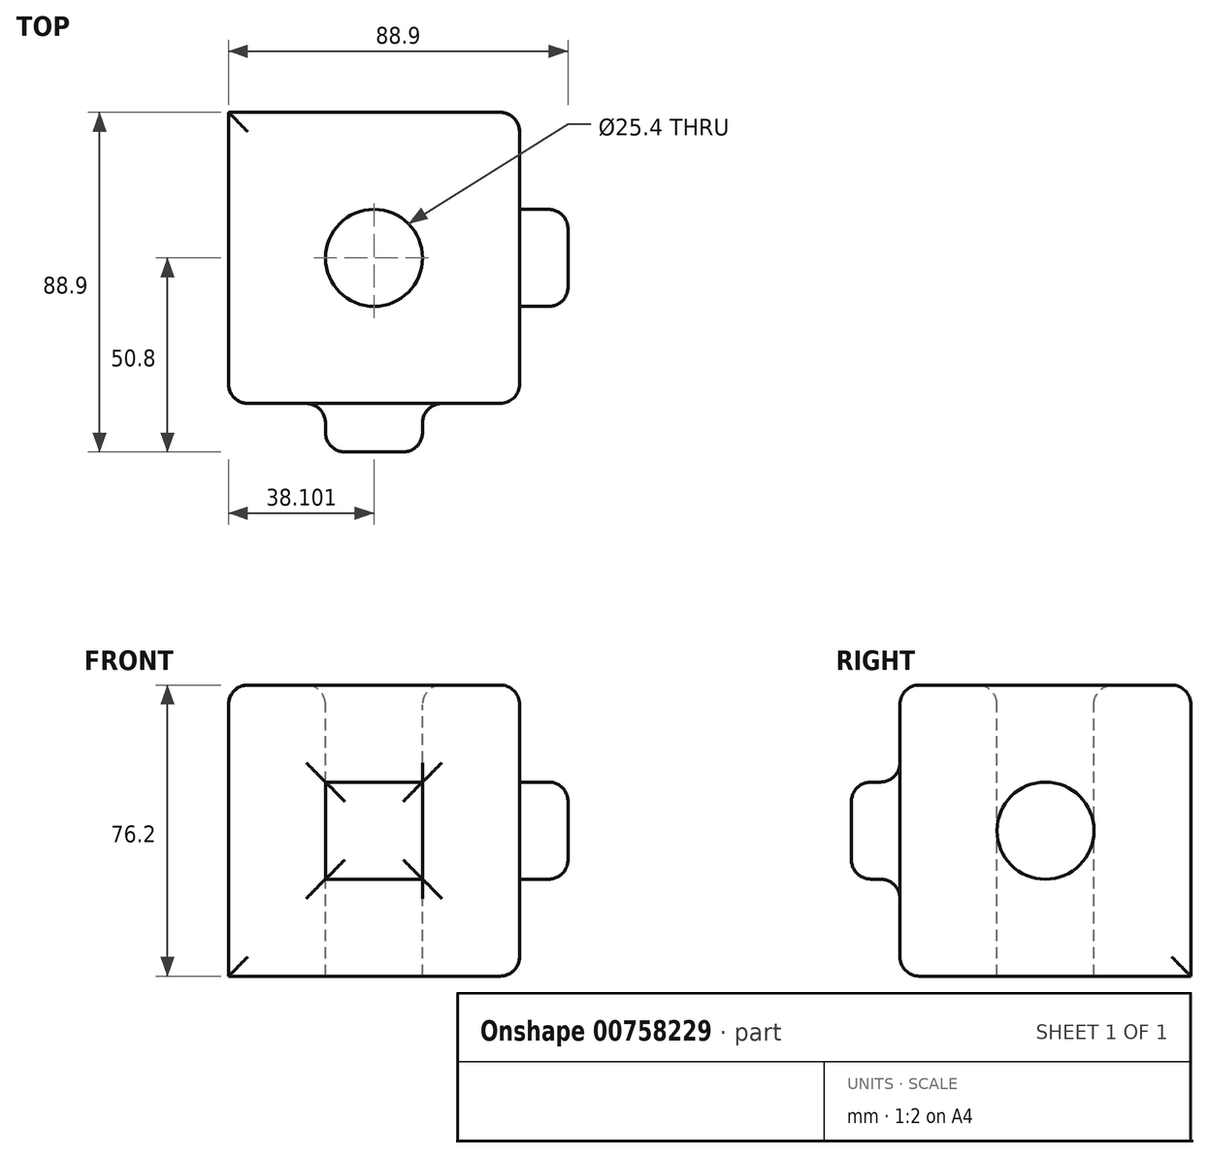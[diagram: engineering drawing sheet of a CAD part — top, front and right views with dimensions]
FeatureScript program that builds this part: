
annotation { "Feature Type Name" : "Feature", "Feature Type Description" : "" }
export const myFeature = defineFeature(function(context is Context, id is Id, definition is map)
    precondition{}
    {
        {
            var Q0;
            Q0=qCreatedBy(makeId("Front.planeOp"),FACE);
            var sketch = newSketch(context, id + "F0", { "sketchPlane" : qUnion([Q0])});
            skLineSegment(sketch, "E0.bottom", {"start": v(-584.28, 76.45) * mm, "end": v(-508.08, 76.45) * mm});
            skLineSegment(sketch, "E0.top", {"start": v(-584.28, 152.65) * mm, "end": v(-508.08, 152.65) * mm});
            skLineSegment(sketch, "E0.left", {"start": v(-584.28, 76.45) * mm, "end": v(-584.28, 152.65) * mm});
            skLineSegment(sketch, "E0.right", {"start": v(-508.08, 76.45) * mm, "end": v(-508.08, 152.65) * mm});
            skSolve(sketch);
        }
        {
            var Q0;
            Q0 = qSketchRegion(id + "F0", true);
            extrude(context, id + "F1", {"entities" : qUnion([Q0]), "depth" : 76.2 * mm, "offsetDistance" : 25.4 * mm});
        }
        {
            var Q0;
            Q0=makeQuery(id+"F1.opExtrude","SWEPT_FACE",FACE,{"disambiguationData":[OSD([sQuery(id+"F0.wireOp",EDGE,"E0.top")])]});
            var sketch = newSketch(context, id + "F2", { "sketchPlane" : qUnion([Q0])});
            skPoint(sketch, "E1", {"position": v(-546.18, -38.1) * mm});
            skPoint(sketch, "E1.positionSnap0", {"position": v(-508.08, -38.1) * mm});
            skPoint(sketch, "E1.positionSnap1", {"position": v(-546.18, 0) * mm});
            skSolve(sketch);
        }
        {
            var Q0;
            Q0=sQuery(id+"F2.wireOp",VERTEX,"E1");
            var Q1;
            Q1=makeQuery(id+"F1.opExtrude","SWEPT_BODY",BODY,{"disambiguationData":[OSD([sQuery(id+"F0.wireOp",EDGE,"E0.bottom"),sQuery(id+"F0.wireOp",EDGE,"E0.top"),sQuery(id+"F0.wireOp",EDGE,"E0.left"),sQuery(id+"F0.wireOp",EDGE,"E0.right")])]});
            hole(context, id + "F3", {"style" : HoleStyle.SIMPLE, "endStyle" : HoleEndStyle.THROUGH, "holeDiameter" : 25.4 * mm, "majorDiameter" : 6.35 * mm, "isTappedThrough" : true, "tappedDepth" : 12.7 * mm, "tapClearance" : 3, "locations" : qUnion([Q0]), "scope" : qUnion([Q1])});
        }
        {
            var Q0;
            Q0=makeQuery(id+"F1.opExtrude","CAP_FACE",FACE,{"disambiguationData":[OSD([sQuery(id+"F0.wireOp",EDGE,"E0.bottom"),sQuery(id+"F0.wireOp",EDGE,"E0.top"),sQuery(id+"F0.wireOp",EDGE,"E0.left"),sQuery(id+"F0.wireOp",EDGE,"E0.right")])],"isStart":false});
            var sketch = newSketch(context, id + "F4", { "sketchPlane" : qUnion([Q0])});
            skPoint(sketch, "E2", {"position": v(-546.18, 114.55) * mm});
            skPoint(sketch, "E2.positionSnap0", {"position": v(-508.08, 114.55) * mm});
            skPoint(sketch, "E2.positionSnap1", {"position": v(-546.18, 152.65) * mm});
            skLineSegment(sketch, "E3.bottom", {"start": v(-533.48, 127.25) * mm, "end": v(-558.88, 127.25) * mm});
            skLineSegment(sketch, "E3.top", {"start": v(-533.48, 101.85) * mm, "end": v(-558.88, 101.85) * mm});
            skLineSegment(sketch, "E3.left", {"start": v(-533.48, 127.25) * mm, "end": v(-533.48, 101.85) * mm});
            skLineSegment(sketch, "E3.right", {"start": v(-558.88, 127.25) * mm, "end": v(-558.88, 101.85) * mm});
            skSolve(sketch);
        }
        {
            var Q0;
            Q0 = qSketchRegion(id + "F4", true);
            extrude(context, id + "F5", {"entities" : qUnion([Q0]), "operationType" : NewBodyOperationType.ADD, "depth" : 12.7 * mm, "offsetDistance" : 25.4 * mm});
        }
        {
            var Q0;
            Q0=makeQuery(id+"F1.opExtrude","SWEPT_FACE",FACE,{"disambiguationData":[OSD([sQuery(id+"F0.wireOp",EDGE,"E0.right")])]});
            var sketch = newSketch(context, id + "F6", { "sketchPlane" : qUnion([Q0])});
            skPoint(sketch, "E4", {"position": v(-38.1, 114.55) * mm});
            skPoint(sketch, "E4.positionSnap0", {"position": v(0, 114.55) * mm});
            skPoint(sketch, "E4.positionSnap1", {"position": v(-38.1, 152.65) * mm});
            skCircle(sketch, "E5", {"center": v(-38.1, 114.55) * mm, "radius": 12.7 * mm});
            skSolve(sketch);
        }
        {
            var Q0;
            Q0 = qSketchRegion(id + "F6", true);
            extrude(context, id + "F7", {"entities" : qUnion([Q0]), "operationType" : NewBodyOperationType.ADD, "depth" : 12.7 * mm, "offsetDistance" : 25.4 * mm});
        }
        {
            var Q0;
            Q0=makeQuery(id+"F1.opExtrude","CAP_EDGE",EDGE,{"disambiguationData":[OSD([sQuery(id+"F0.wireOp",EDGE,"E0.top")])],"isStart":false});
            var Q1;
            Q1=makeQuery(id+"F1.opExtrude","SWEPT_EDGE",EDGE,{"disambiguationData":[OSD([sQuery(id+"F0.wireOp",EDGE,"E0.top"),sQuery(id+"F0.wireOp",EDGE,"E0.left")])]});
            var Q2;
            Q2=makeQuery(id+"F5.opExtrude","CAP_EDGE",EDGE,{"disambiguationData":[OSD([sQuery(id+"F4.wireOp",EDGE,"E3.bottom")])],"isStart":false});
            var Q3;
            Q3=makeQuery(id+"F5.opExtrude","CAP_EDGE",EDGE,{"disambiguationData":[OSD([sQuery(id+"F4.wireOp",EDGE,"E3.left")])],"isStart":false});
            var Q4;
            Q4=makeQuery(id+"F5.opExtrude","CAP_EDGE",EDGE,{"disambiguationData":[OSD([sQuery(id+"F4.wireOp",EDGE,"E3.top")])],"isStart":false});
            var Q5;
            Q5=makeQuery(id+"F5.opExtrude","CAP_EDGE",EDGE,{"disambiguationData":[OSD([sQuery(id+"F4.wireOp",EDGE,"E3.right")])],"isStart":false});
            var Q6;
            Q6=makeQuery(id+"F7.opExtrude","CAP_EDGE",EDGE,{"disambiguationData":[OSD([sQuery(id+"F6.wireOp",EDGE,"E5")])],"isStart":true});
            var Q7;
            Q7=makeQuery(id+"F7.opExtrude","CAP_EDGE",EDGE,{"disambiguationData":[OSD([sQuery(id+"F6.wireOp",EDGE,"E5")])],"isStart":false});
            var Q8;
            Q8=makeQuery(id+"F3.hole-0.boolean.opBoolean","COPY",EDGE,{"derivedFrom":makeQuery(id+"F3.hole-0.opRevolve","SWEPT_EDGE",EDGE,{"disambiguationData":[OSD([sQuery(id+"F3.hole-0.sketch.wireOp",EDGE,"core_line_2"),sQuery(id+"F3.hole-0.sketch.wireOp",EDGE,"core_line_3")])]})});
            var Q9;
            Q9=makeQuery(id+"F1.opExtrude","CAP_EDGE",EDGE,{"disambiguationData":[OSD([sQuery(id+"F0.wireOp",EDGE,"E0.left")])],"isStart":false});
            var Q10;
            Q10=makeQuery(id+"F1.opExtrude","CAP_FACE",FACE,{"disambiguationData":[OSD([sQuery(id+"F0.wireOp",EDGE,"E0.bottom"),sQuery(id+"F0.wireOp",EDGE,"E0.top"),sQuery(id+"F0.wireOp",EDGE,"E0.left"),sQuery(id+"F0.wireOp",EDGE,"E0.right")])],"isStart":false});
            var Q11;
            Q11=makeQuery(id+"F1.opExtrude","SWEPT_EDGE",EDGE,{"disambiguationData":[OSD([sQuery(id+"F0.wireOp",EDGE,"E0.top"),sQuery(id+"F0.wireOp",EDGE,"E0.right")])]});
            var Q12;
            Q12=makeQuery(id+"F1.opExtrude","CAP_EDGE",EDGE,{"disambiguationData":[OSD([sQuery(id+"F0.wireOp",EDGE,"E0.right")])],"isStart":true});
            var Q13;
            Q13=makeQuery(id+"F1.opExtrude","SWEPT_EDGE",EDGE,{"disambiguationData":[OSD([sQuery(id+"F0.wireOp",EDGE,"E0.bottom"),sQuery(id+"F0.wireOp",EDGE,"E0.right")])]});
            var Q14;
            Q14=makeQuery(id+"F1.opExtrude","CAP_EDGE",EDGE,{"disambiguationData":[OSD([sQuery(id+"F0.wireOp",EDGE,"E0.top")])],"isStart":true});
            var Q15;
            Q15=makeQuery(id+"F1.opExtrude","SWEPT_FACE",FACE,{"disambiguationData":[OSD([sQuery(id+"F0.wireOp",EDGE,"E0.top")])]});
            fillet(context, id + "F8", {"entities" : qUnion([Q0, Q1, Q2, Q3, Q4, Q5, Q6, Q7, Q8, Q9, Q10, Q11, Q12, Q13, Q14, Q15]), "radius" : 5.08 * mm, "tangentPropagation" : true, "allowEdgeOverflow" : false});
        }
    });
